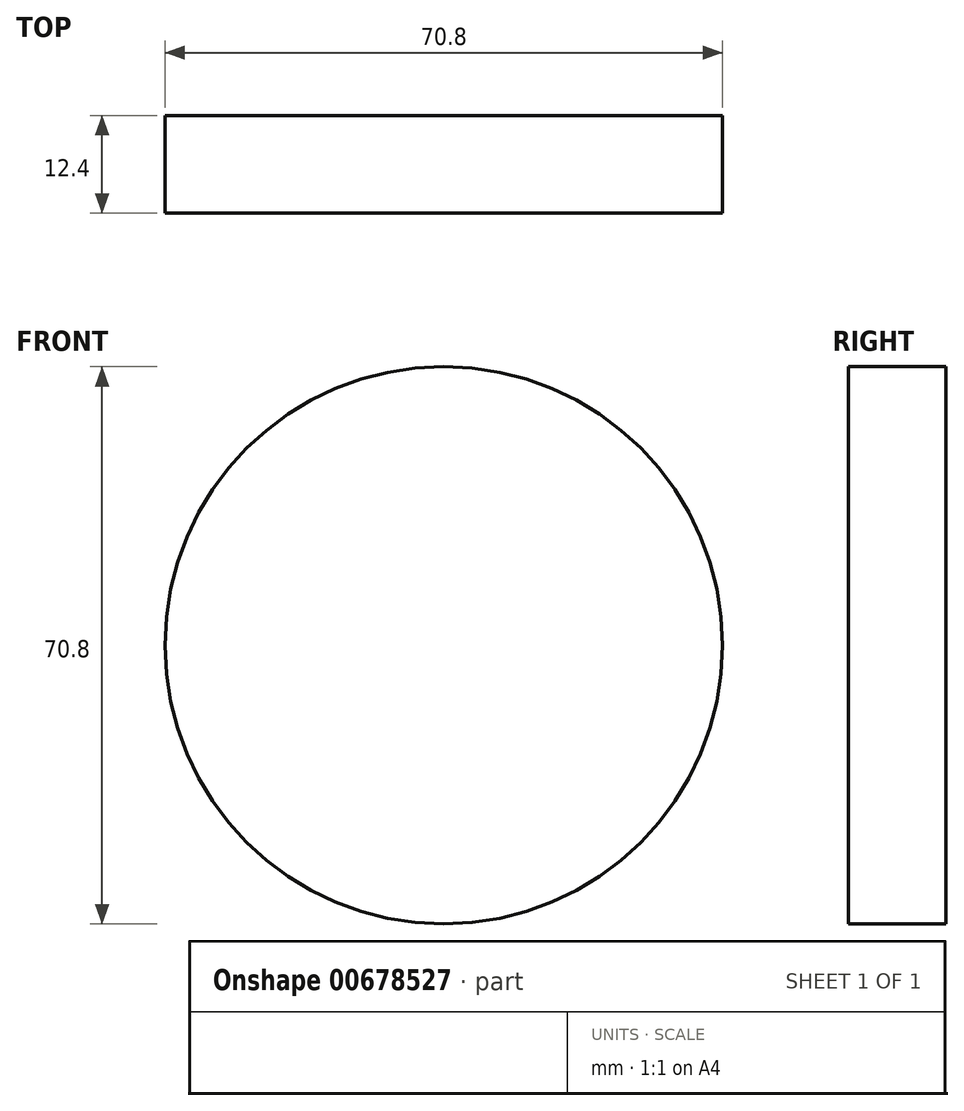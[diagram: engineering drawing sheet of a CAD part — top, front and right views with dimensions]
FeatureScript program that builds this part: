
annotation { "Feature Type Name" : "Feature", "Feature Type Description" : "" }
export const myFeature = defineFeature(function(context is Context, id is Id, definition is map)
    precondition{}
    {
        {
            var Q0;
            Q0=qCreatedBy(makeId("Front.planeOp"),FACE);
            var sketch = newSketch(context, id + "F0", { "sketchPlane" : qUnion([Q0])});
            skCircle(sketch, "E0", {"center": v(0, 0) * mm, "radius": 26.86 * mm});
            skCircle(sketch, "E1", {"center": v(0.14, 0.43) * mm, "radius": 35.4 * mm});
            skSolve(sketch);
        }
        {
            var Q0;
            Q0=makeQuery(id+"F0.imprint","IMPRINT",FACE,{"disambiguationData":[TD([[makeQuery(id+"F0.imprint","IMPRINT",EDGE,{"derivedFrom":sQuery(id+"F0.wireOp",EDGE,"E0")}),1.0]])]});
            var Q1;
            Q1=makeQuery(id+"F0.imprint","IMPRINT",FACE,{"disambiguationData":[TD([[makeQuery(id+"F0.imprint","IMPRINT",EDGE,{"derivedFrom":sQuery(id+"F0.wireOp",EDGE,"E0")}),-1.0]])]});
            extrude(context, id + "F1", {"entities" : qUnion([Q0, Q1]), "depth" : 12.4 * mm, "offsetDistance" : 25 * mm});
        }
    });
